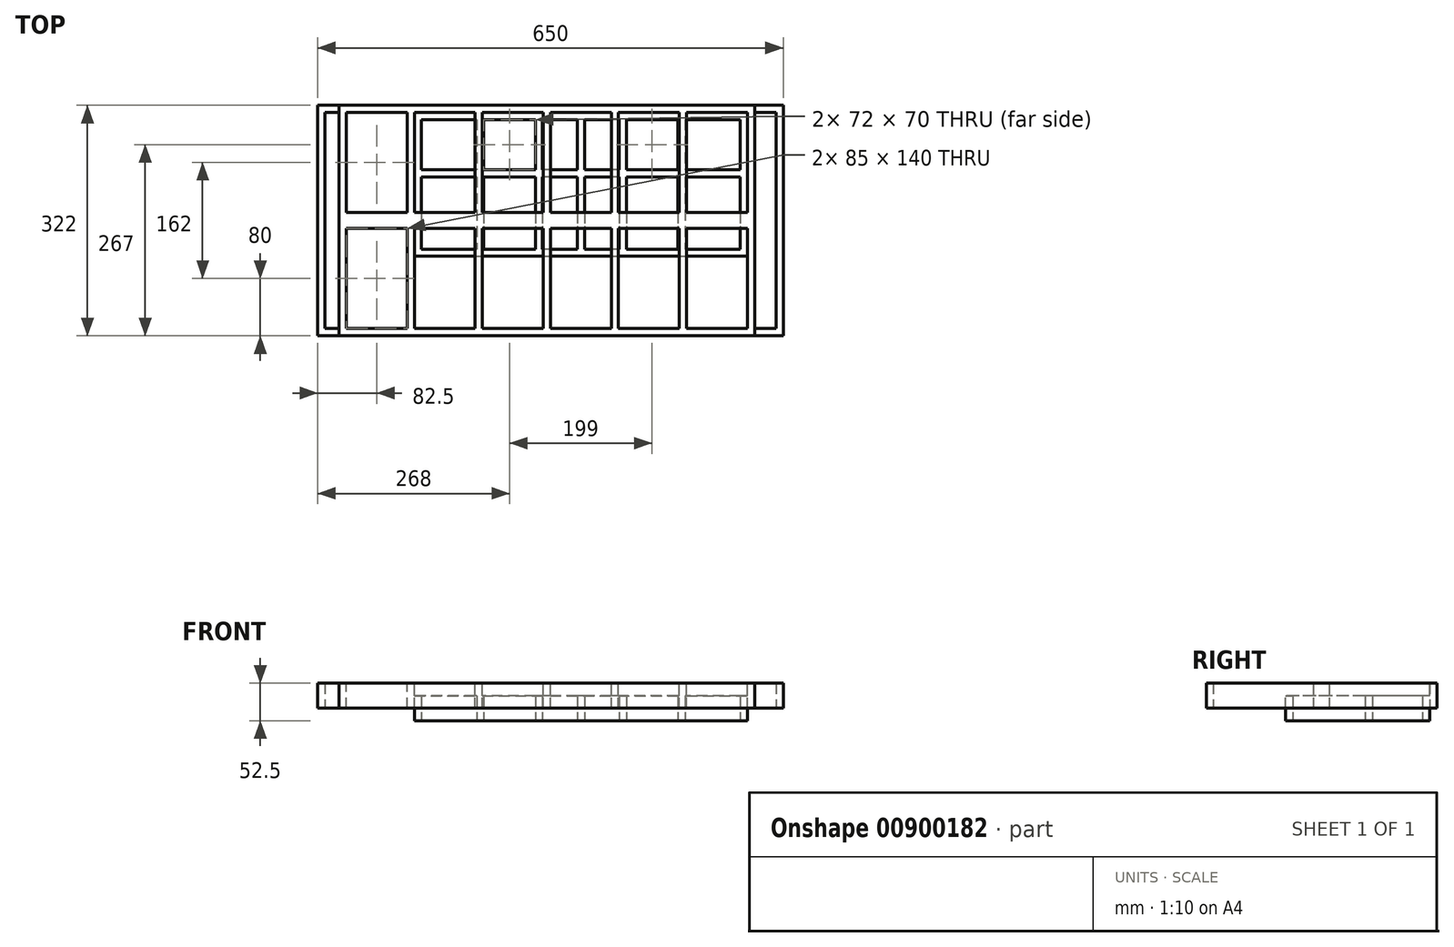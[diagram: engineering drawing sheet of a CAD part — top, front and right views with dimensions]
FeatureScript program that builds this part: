
annotation { "Feature Type Name" : "Feature", "Feature Type Description" : "" }
export const myFeature = defineFeature(function(context is Context, id is Id, definition is map)
    precondition{}
    {
        {
            var Q0;
            Q0=qCreatedBy(makeId("Top.planeOp"),FACE);
            var sketch = newSketch(context, id + "F0", { "sketchPlane" : qUnion([Q0])});
            skLineSegment(sketch, "E0.bottom", {"start": v(-290, 161) * mm, "end": v(290, 161) * mm});
            skLineSegment(sketch, "E0.top", {"start": v(-290, -161) * mm, "end": v(290, -161) * mm});
            skLineSegment(sketch, "E0.left", {"start": v(-290, 161) * mm, "end": v(-290, -161) * mm});
            skLineSegment(sketch, "E0.right", {"start": v(290, 161) * mm, "end": v(290, -161) * mm});
            skPoint(sketch, "E0.middle", {"position": v(0, 0) * mm});
            skSolve(sketch);
        }
        {
            var Q0;
            Q0=qSketchRegion(id+"F0",true);
            extrude(context, id + "F1", {"entities" : qUnion([Q0]), "depth" : 35 * mm, "offsetDistance" : 25 * mm, "symmetric" : true});
        }
        {
            var Q0;
            Q0=qCreatedBy(makeId("Top.planeOp"),FACE);
            var sketch = newSketch(context, id + "F2", { "sketchPlane" : qUnion([Q0])});
            skLineSegment(sketch, "E1.bottom", {"start": v(195, -11) * mm, "end": v(280, -11) * mm});
            skLineSegment(sketch, "E1.top", {"start": v(195, -151) * mm, "end": v(280, -151) * mm});
            skLineSegment(sketch, "E1.left", {"start": v(195, -11) * mm, "end": v(195, -151) * mm});
            skLineSegment(sketch, "E1.right", {"start": v(280, -11) * mm, "end": v(280, -151) * mm});
            skLineSegment(sketch, "E2.1.0.0", {"start": v(100, -11) * mm, "end": v(185, -11) * mm});
            skLineSegment(sketch, "E2.1.0.1", {"start": v(100, -11) * mm, "end": v(100, -151) * mm});
            skLineSegment(sketch, "E2.1.0.2", {"start": v(185, -11) * mm, "end": v(185, -151) * mm});
            skLineSegment(sketch, "E2.1.0.3", {"start": v(100, -151) * mm, "end": v(185, -151) * mm});
            skLineSegment(sketch, "E2.2.0.0", {"start": v(5, -11) * mm, "end": v(90, -11) * mm});
            skLineSegment(sketch, "E2.2.0.1", {"start": v(5, -11) * mm, "end": v(5, -151) * mm});
            skLineSegment(sketch, "E2.2.0.2", {"start": v(90, -11) * mm, "end": v(90, -151) * mm});
            skLineSegment(sketch, "E2.2.0.3", {"start": v(5, -151) * mm, "end": v(90, -151) * mm});
            skLineSegment(sketch, "E2.3.0.0", {"start": v(-90, -11) * mm, "end": v(-5, -11) * mm});
            skLineSegment(sketch, "E2.3.0.1", {"start": v(-90, -11) * mm, "end": v(-90, -151) * mm});
            skLineSegment(sketch, "E2.3.0.2", {"start": v(-5, -11) * mm, "end": v(-5, -151) * mm});
            skLineSegment(sketch, "E2.3.0.3", {"start": v(-90, -151) * mm, "end": v(-5, -151) * mm});
            skLineSegment(sketch, "E2.4.0.0", {"start": v(-185, -11) * mm, "end": v(-100, -11) * mm});
            skLineSegment(sketch, "E2.4.0.1", {"start": v(-185, -11) * mm, "end": v(-185, -151) * mm});
            skLineSegment(sketch, "E2.4.0.2", {"start": v(-100, -11) * mm, "end": v(-100, -151) * mm});
            skLineSegment(sketch, "E2.4.0.3", {"start": v(-185, -151) * mm, "end": v(-100, -151) * mm});
            skLineSegment(sketch, "E2.direction1", {"start": v(195, -151) * mm, "end": v(100, -151) * mm, "construction": true});
            skLineSegment(sketch, "E3", {"start": v(-290, 0) * mm, "end": v(290, 0) * mm, "construction": true});
            skLineSegment(sketch, "E4.MirrorCS", {"start": v(100, 151) * mm, "end": v(185, 151) * mm});
            skLineSegment(sketch, "E5.MirrorCS", {"start": v(280, 11) * mm, "end": v(280, 151) * mm});
            skLineSegment(sketch, "E6.MirrorCS", {"start": v(5, 11) * mm, "end": v(5, 151) * mm});
            skLineSegment(sketch, "E7.MirrorCS", {"start": v(-185, 11) * mm, "end": v(-100, 11) * mm});
            skLineSegment(sketch, "E8.MirrorCS", {"start": v(-185, 11) * mm, "end": v(-185, 151) * mm});
            skLineSegment(sketch, "E9.MirrorCS", {"start": v(195, 151) * mm, "end": v(280, 151) * mm});
            skLineSegment(sketch, "E10.MirrorCS", {"start": v(-100, 11) * mm, "end": v(-100, 151) * mm});
            skLineSegment(sketch, "E11.MirrorCS", {"start": v(100, 11) * mm, "end": v(185, 11) * mm});
            skLineSegment(sketch, "E12.MirrorCS", {"start": v(185, 11) * mm, "end": v(185, 151) * mm});
            skLineSegment(sketch, "E13.MirrorCS", {"start": v(195, 11) * mm, "end": v(280, 11) * mm});
            skLineSegment(sketch, "E14.MirrorCS", {"start": v(-90, 11) * mm, "end": v(-90, 151) * mm});
            skLineSegment(sketch, "E15.MirrorCS", {"start": v(90, 11) * mm, "end": v(90, 151) * mm});
            skLineSegment(sketch, "E16.MirrorCS", {"start": v(195, 151) * mm, "end": v(100, 151) * mm, "construction": true});
            skLineSegment(sketch, "E17.MirrorCS", {"start": v(100, 11) * mm, "end": v(100, 151) * mm});
            skLineSegment(sketch, "E18.MirrorCS", {"start": v(-90, 11) * mm, "end": v(-5, 11) * mm});
            skLineSegment(sketch, "E19.MirrorCS", {"start": v(-185, 151) * mm, "end": v(-100, 151) * mm});
            skLineSegment(sketch, "E20.MirrorCS", {"start": v(5, 11) * mm, "end": v(90, 11) * mm});
            skLineSegment(sketch, "E21.MirrorCS", {"start": v(-5, 11) * mm, "end": v(-5, 151) * mm});
            skLineSegment(sketch, "E22.MirrorCS", {"start": v(195, 11) * mm, "end": v(195, 151) * mm});
            skLineSegment(sketch, "E23.MirrorCS", {"start": v(-90, 151) * mm, "end": v(-5, 151) * mm});
            skLineSegment(sketch, "E24.MirrorCS", {"start": v(5, 151) * mm, "end": v(90, 151) * mm});
            skLineSegment(sketch, "E25", {"start": v(-280, 161) * mm, "end": v(-280, -161) * mm, "construction": true});
            skLineSegment(sketch, "E26.bottom", {"start": v(-280, 151) * mm, "end": v(-195, 151) * mm});
            skLineSegment(sketch, "E26.top", {"start": v(-280, 11) * mm, "end": v(-195, 11) * mm});
            skLineSegment(sketch, "E26.left", {"start": v(-280, 151) * mm, "end": v(-280, 11) * mm});
            skLineSegment(sketch, "E26.right", {"start": v(-195, 151) * mm, "end": v(-195, 11) * mm});
            skLineSegment(sketch, "E27.bottom", {"start": v(-280, -11) * mm, "end": v(-195, -11) * mm});
            skLineSegment(sketch, "E27.top", {"start": v(-280, -151) * mm, "end": v(-195, -151) * mm});
            skLineSegment(sketch, "E27.left", {"start": v(-280, -11) * mm, "end": v(-280, -151) * mm});
            skLineSegment(sketch, "E27.right", {"start": v(-195, -11) * mm, "end": v(-195, -151) * mm});
            skLineSegment(sketch, "E28", {"start": v(-185, 151) * mm, "end": v(-290, 151) * mm, "construction": true});
            skLineSegment(sketch, "E29", {"start": v(-185, -151) * mm, "end": v(-290, -151) * mm, "construction": true});
            skLineSegment(sketch, "E30", {"start": v(-195, 151) * mm, "end": v(-195, -151) * mm, "construction": true});
            skPoint(sketch, "E31", {"position": v(-280, 151) * mm});
            skPoint(sketch, "E32", {"position": v(-280, -151) * mm});
            skLineSegment(sketch, "E33", {"start": v(-290, 11) * mm, "end": v(-195, 11) * mm, "construction": true});
            skLineSegment(sketch, "E34", {"start": v(-290, -11) * mm, "end": v(-195, -11) * mm, "construction": true});
            skPoint(sketch, "E35", {"position": v(-280, -11) * mm});
            skSolve(sketch);
        }
        {
            var Q0;
            Q0=qSketchRegion(id+"F2",true);
            extrude(context, id + "F3", {"entities" : qUnion([Q0]), "operationType" : NewBodyOperationType.REMOVE, "oppositeDirection" : true, "depth" : 50 * mm, "offsetDistance" : 25 * mm, "symmetric" : true});
        }
        {
            var Q0;
            Q0=qCreatedBy(makeId("Top.planeOp"),FACE);
            var sketch = newSketch(context, id + "F4", { "sketchPlane" : qUnion([Q0])});
            skLineSegment(sketch, "E36.bottom", {"start": v(-185, 151) * mm, "end": v(280, 151) * mm});
            skLineSegment(sketch, "E36.top", {"start": v(-185, -50) * mm, "end": v(280, -50) * mm});
            skLineSegment(sketch, "E36.left", {"start": v(-185, 151) * mm, "end": v(-185, -50) * mm});
            skLineSegment(sketch, "E36.right", {"start": v(280, 151) * mm, "end": v(280, -50) * mm});
            skLineSegment(sketch, "E37.bottom", {"start": v(280, 151) * mm, "end": v(-185, 151) * mm});
            skLineSegment(sketch, "E37.top", {"start": v(280, -50) * mm, "end": v(-185, -50) * mm});
            skLineSegment(sketch, "E37.left", {"start": v(280, 120) * mm, "end": v(280, -50) * mm});
            skLineSegment(sketch, "E38", {"start": v(280, 151) * mm, "end": v(280, 151) * mm});
            skSolve(sketch);
        }
        {
            var Q0;
            Q0=qSketchRegion(id+"F4",true);
            extrude(context, id + "F5", {"entities" : qUnion([Q0]), "operationType" : NewBodyOperationType.ADD, "oppositeDirection" : true, "depth" : 35 * mm, "offsetDistance" : 25 * mm});
        }
        {
            var Q0;
            Q0=makeQuery(id+"F5.opExtrude","CAP_FACE",FACE,{"disambiguationData":[OSD([sQuery(id+"F4.wireOp",EDGE,"E37.bottom"),sQuery(id+"F4.wireOp",EDGE,"E37.top"),sQuery(id+"F4.wireOp",EDGE,"E37.left"),sQuery(id+"F4.wireOp",EDGE,"E36.left")])],"isStart":false});
            var sketch = newSketch(context, id + "F6", { "sketchPlane" : qUnion([Q0])});
            skLineSegment(sketch, "E39.bottom", {"start": v(270, -141) * mm, "end": v(193, -141) * mm});
            skLineSegment(sketch, "E39.top", {"start": v(270, 40) * mm, "end": v(193, 40) * mm});
            skLineSegment(sketch, "E39.left", {"start": v(270, -141) * mm, "end": v(270, -71) * mm});
            skLineSegment(sketch, "E39.right", {"start": v(-175, -141) * mm, "end": v(-175, -71) * mm});
            skLineSegment(sketch, "E40", {"start": v(106, -141) * mm, "end": v(106, 40) * mm, "construction": true});
            skLineSegment(sketch, "E41", {"start": v(-11, -141) * mm, "end": v(-11, 40) * mm, "construction": true});
            skLineSegment(sketch, "E42", {"start": v(47.5, -141) * mm, "end": v(47.5, 40) * mm, "construction": true});
            skLineSegment(sketch, "E43", {"start": v(188, -141) * mm, "end": v(188, 40) * mm, "construction": true});
            skLineSegment(sketch, "E44", {"start": v(193, -141) * mm, "end": v(193, -71) * mm});
            skLineSegment(sketch, "E45.MirrorCS", {"start": v(183, -141) * mm, "end": v(183, -71) * mm});
            skLineSegment(sketch, "E46", {"start": v(111, -141) * mm, "end": v(111, -71) * mm});
            skLineSegment(sketch, "E47", {"start": v(52.5, -141) * mm, "end": v(52.5, -71) * mm});
            skLineSegment(sketch, "E48", {"start": v(-98, -141) * mm, "end": v(-98, -71) * mm});
            skLineSegment(sketch, "E49", {"start": v(-16, -141) * mm, "end": v(-16, -71) * mm});
            skLineSegment(sketch, "E50.MirrorCS", {"start": v(-88, -141) * mm, "end": v(-88, -71) * mm});
            skLineSegment(sketch, "E51.MirrorCS", {"start": v(-6, -141) * mm, "end": v(-6, -71) * mm});
            skLineSegment(sketch, "E52.MirrorCS", {"start": v(42.5, -141) * mm, "end": v(42.5, -71) * mm});
            skLineSegment(sketch, "E53.MirrorCS", {"start": v(101, -141) * mm, "end": v(101, -71) * mm});
            skLineSegment(sketch, "E54.trimOffspring", {"start": v(183, -141) * mm, "end": v(111, -141) * mm});
            skLineSegment(sketch, "E55.trimOffspring", {"start": v(101, -141) * mm, "end": v(52.5, -141) * mm});
            skLineSegment(sketch, "E56.trimOffspring", {"start": v(42.5, -141) * mm, "end": v(-6, -141) * mm});
            skLineSegment(sketch, "E57.trimOffspring", {"start": v(-16, -141) * mm, "end": v(-88, -141) * mm});
            skLineSegment(sketch, "E58.trimOffspring", {"start": v(183, 40) * mm, "end": v(111, 40) * mm});
            skLineSegment(sketch, "E59.trimOffspring", {"start": v(101, 40) * mm, "end": v(52.5, 40) * mm});
            skLineSegment(sketch, "E60.trimOffspring", {"start": v(42.5, 40) * mm, "end": v(-6, 40) * mm});
            skLineSegment(sketch, "E61.trimOffspring", {"start": v(-16, 40) * mm, "end": v(-88, 40) * mm});
            skLineSegment(sketch, "E62.trimOffspring", {"start": v(-98, -141) * mm, "end": v(-175, -141) * mm});
            skLineSegment(sketch, "E63.trimOffspring", {"start": v(-98, 40) * mm, "end": v(-175, 40) * mm});
            skLineSegment(sketch, "E64", {"start": v(270, -71) * mm, "end": v(193, -71) * mm});
            skLineSegment(sketch, "E65.MirrorCS", {"start": v(270, -61) * mm, "end": v(193, -61) * mm});
            skLineSegment(sketch, "E66.trimOffspring", {"start": v(270, -61) * mm, "end": v(270, 40) * mm});
            skLineSegment(sketch, "E67.trimOffspring", {"start": v(193, -61) * mm, "end": v(193, 40) * mm});
            skLineSegment(sketch, "E68.trimOffspring", {"start": v(183, -71) * mm, "end": v(111, -71) * mm});
            skLineSegment(sketch, "E69.trimOffspring", {"start": v(183, -61) * mm, "end": v(183, 40) * mm});
            skLineSegment(sketch, "E70.trimOffspring", {"start": v(111, -61) * mm, "end": v(111, 40) * mm});
            skLineSegment(sketch, "E71.trimOffspring", {"start": v(101, -71) * mm, "end": v(52.5, -71) * mm});
            skLineSegment(sketch, "E72.trimOffspring", {"start": v(101, -61) * mm, "end": v(101, 40) * mm});
            skLineSegment(sketch, "E73.trimOffspring", {"start": v(52.5, -61) * mm, "end": v(52.5, 40) * mm});
            skLineSegment(sketch, "E74.trimOffspring", {"start": v(42.5, -71) * mm, "end": v(-6, -71) * mm});
            skLineSegment(sketch, "E75.trimOffspring", {"start": v(42.5, -61) * mm, "end": v(-6, -61) * mm});
            skLineSegment(sketch, "E76.trimOffspring", {"start": v(42.5, -61) * mm, "end": v(42.5, 40) * mm});
            skLineSegment(sketch, "E77.trimOffspring", {"start": v(-6, -61) * mm, "end": v(-6, 40) * mm});
            skLineSegment(sketch, "E78.trimOffspring", {"start": v(-16, -71) * mm, "end": v(-88, -71) * mm});
            skLineSegment(sketch, "E79.trimOffspring", {"start": v(-16, -61) * mm, "end": v(-16, 40) * mm});
            skLineSegment(sketch, "E80.trimOffspring", {"start": v(-16, -61) * mm, "end": v(-88, -61) * mm});
            skLineSegment(sketch, "E81.trimOffspring", {"start": v(-98, -61) * mm, "end": v(-98, 40) * mm});
            skLineSegment(sketch, "E82.trimOffspring", {"start": v(-98, -71) * mm, "end": v(-175, -71) * mm});
            skLineSegment(sketch, "E83.trimOffspring", {"start": v(-88, -61) * mm, "end": v(-88, 40) * mm});
            skLineSegment(sketch, "E84.trimOffspring", {"start": v(-98, -61) * mm, "end": v(-175, -61) * mm});
            skLineSegment(sketch, "E85.trimOffspring", {"start": v(-175, -61) * mm, "end": v(-175, 40) * mm});
            skLineSegment(sketch, "E86.trimOffspring", {"start": v(183, -61) * mm, "end": v(111, -61) * mm});
            skLineSegment(sketch, "E87.trimOffspring", {"start": v(101, -61) * mm, "end": v(52.5, -61) * mm});
            skSolve(sketch);
        }
        {
            var Q0;
            Q0=qSketchRegion(id+"F6",true);
            extrude(context, id + "F7", {"entities" : qUnion([Q0]), "operationType" : NewBodyOperationType.REMOVE, "oppositeDirection" : true, "depth" : 35 * mm, "offsetDistance" : 25 * mm});
        }
        {
            var Q0;
            Q0=makeQuery(id+"F1.opExtrude","SWEPT_FACE",FACE,{"disambiguationData":[OSD([sQuery(id+"F0.wireOp",EDGE,"E0.left")])]});
            var sketch = newSketch(context, id + "F8", { "sketchPlane" : qUnion([Q0])});
            skLineSegment(sketch, "E88.bottom", {"start": v(-161, -17.5) * mm, "end": v(161, -17.5) * mm});
            skLineSegment(sketch, "E88.top", {"start": v(-161, 17.5) * mm, "end": v(161, 17.5) * mm});
            skLineSegment(sketch, "E88.left", {"start": v(-161, -17.5) * mm, "end": v(-161, 17.5) * mm});
            skLineSegment(sketch, "E88.right", {"start": v(161, -17.5) * mm, "end": v(161, 17.5) * mm});
            skPoint(sketch, "E88.middle", {"position": v(0, 0) * mm});
            skSolve(sketch);
        }
        {
            var Q0;
            Q0=qSketchRegion(id+"F8",true);
            extrude(context, id + "F9", {"entities" : qUnion([Q0]), "depth" : 30 * mm, "offsetDistance" : 25 * mm});
        }
        {
            var Q0;
            Q0=makeQuery(id+"F9.opExtrude","SWEPT_FACE",FACE,{"disambiguationData":[OSD([sQuery(id+"F8.wireOp",EDGE,"E88.bottom")])]});
            var sketch = newSketch(context, id + "F10", { "sketchPlane" : qUnion([Q0])});
            skLineSegment(sketch, "E89.bottom", {"start": v(-290, -151) * mm, "end": v(-310, -151) * mm});
            skLineSegment(sketch, "E89.top", {"start": v(-290, 151) * mm, "end": v(-310, 151) * mm});
            skLineSegment(sketch, "E89.left", {"start": v(-290, -151) * mm, "end": v(-290, 151) * mm});
            skLineSegment(sketch, "E89.right", {"start": v(-310, -151) * mm, "end": v(-310, 151) * mm});
            skSolve(sketch);
        }
        {
            var Q0;
            Q0=qSketchRegion(id+"F10",true);
            extrude(context, id + "F11", {"entities" : qUnion([Q0]), "operationType" : NewBodyOperationType.REMOVE, "endBound" : BoundingType.THROUGH_ALL, "oppositeDirection" : true, "depth" : 25 * mm, "offsetDistance" : 25 * mm});
        }
        {
            var Q0;
            Q0=makeQuery(id+"F1.opExtrude","SWEPT_FACE",FACE,{"disambiguationData":[OSD([sQuery(id+"F0.wireOp",EDGE,"E0.right")])]});
            var sketch = newSketch(context, id + "F12", { "sketchPlane" : qUnion([Q0])});
            skLineSegment(sketch, "E90.bottom", {"start": v(-161, 17.5) * mm, "end": v(161, 17.5) * mm});
            skLineSegment(sketch, "E90.top", {"start": v(-161, -17.5) * mm, "end": v(161, -17.5) * mm});
            skLineSegment(sketch, "E90.left", {"start": v(-161, 17.5) * mm, "end": v(-161, -17.5) * mm});
            skLineSegment(sketch, "E90.right", {"start": v(161, 17.5) * mm, "end": v(161, -17.5) * mm});
            skPoint(sketch, "E90.middle", {"position": v(0, 0) * mm});
            skSolve(sketch);
        }
        {
            var Q0;
            Q0=qSketchRegion(id+"F12",true);
            extrude(context, id + "F13", {"entities" : qUnion([Q0]), "depth" : 40 * mm, "offsetDistance" : 25 * mm});
        }
        {
            var Q0;
            Q0=makeQuery(id+"F13.opExtrude","SWEPT_FACE",FACE,{"disambiguationData":[OSD([sQuery(id+"F12.wireOp",EDGE,"E90.top")])]});
            var sketch = newSketch(context, id + "F14", { "sketchPlane" : qUnion([Q0])});
            skLineSegment(sketch, "E91", {"start": v(290, 151) * mm, "end": v(320, 151) * mm});
            skLineSegment(sketch, "E92", {"start": v(320, 151) * mm, "end": v(320, -151) * mm});
            skLineSegment(sketch, "E93", {"start": v(320, -151) * mm, "end": v(290, -151) * mm});
            skSolve(sketch);
        }
        {
            var Q0;
            Q0=qSketchRegion(id+"F14",true);
            var Q1;
            {var subQ0=sQuery(id+"F14.wireOp",EDGE,"E91");Q1=makeQuery(id+"F14.imprint","IMPRINT",FACE,{"disambiguationData":[TD([[makeQuery(id+"F14.imprint","IMPRINT",EDGE,{"derivedFrom":subQ0}),-1.0]])]});}
            extrude(context, id + "F15", {"entities" : qUnion([Q0, Q1]), "operationType" : NewBodyOperationType.REMOVE, "endBound" : BoundingType.THROUGH_ALL, "oppositeDirection" : true, "depth" : 25 * mm, "offsetDistance" : 25 * mm});
        }
    });
